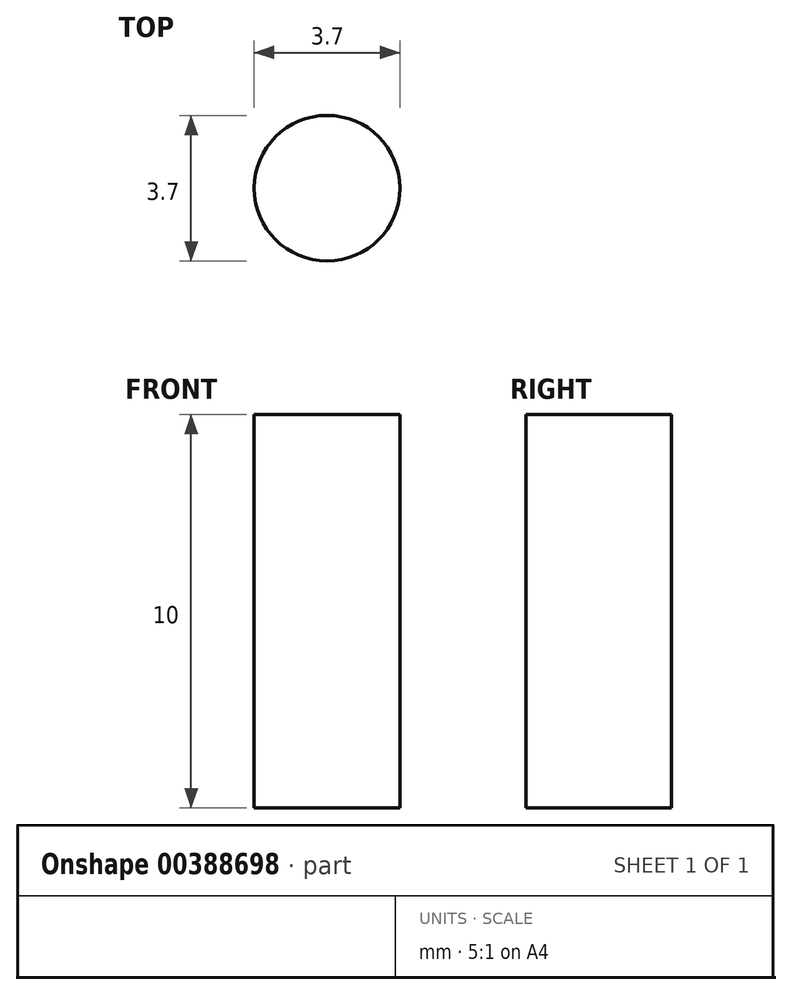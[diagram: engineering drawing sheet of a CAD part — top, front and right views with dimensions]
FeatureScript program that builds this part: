
annotation { "Feature Type Name" : "Feature", "Feature Type Description" : "" }
export const myFeature = defineFeature(function(context is Context, id is Id, definition is map)
    precondition{}
    {
        {
            var Q0;
            Q0=qCreatedBy(makeId("Top.planeOp"),FACE);
            var sketch = newSketch(context, id + "F0", { "sketchPlane" : qUnion([Q0])});
            skCircle(sketch, "E0", {"center": v(0, 0) * mm, "radius": 1.85 * mm});
            skSolve(sketch);
        }
        {
            var Q0;
            Q0=makeQuery(id+"F0.imprint","IMPRINT",FACE,{"disambiguationData":[TD([[makeQuery(id+"F0.imprint","IMPRINT",EDGE,{"derivedFrom":sQuery(id+"F0.wireOp",EDGE,"E0")}),1.0]])]});
            extrude(context, id + "F1", {"entities" : qUnion([Q0]), "depth" : 10 * mm});
        }
    });
